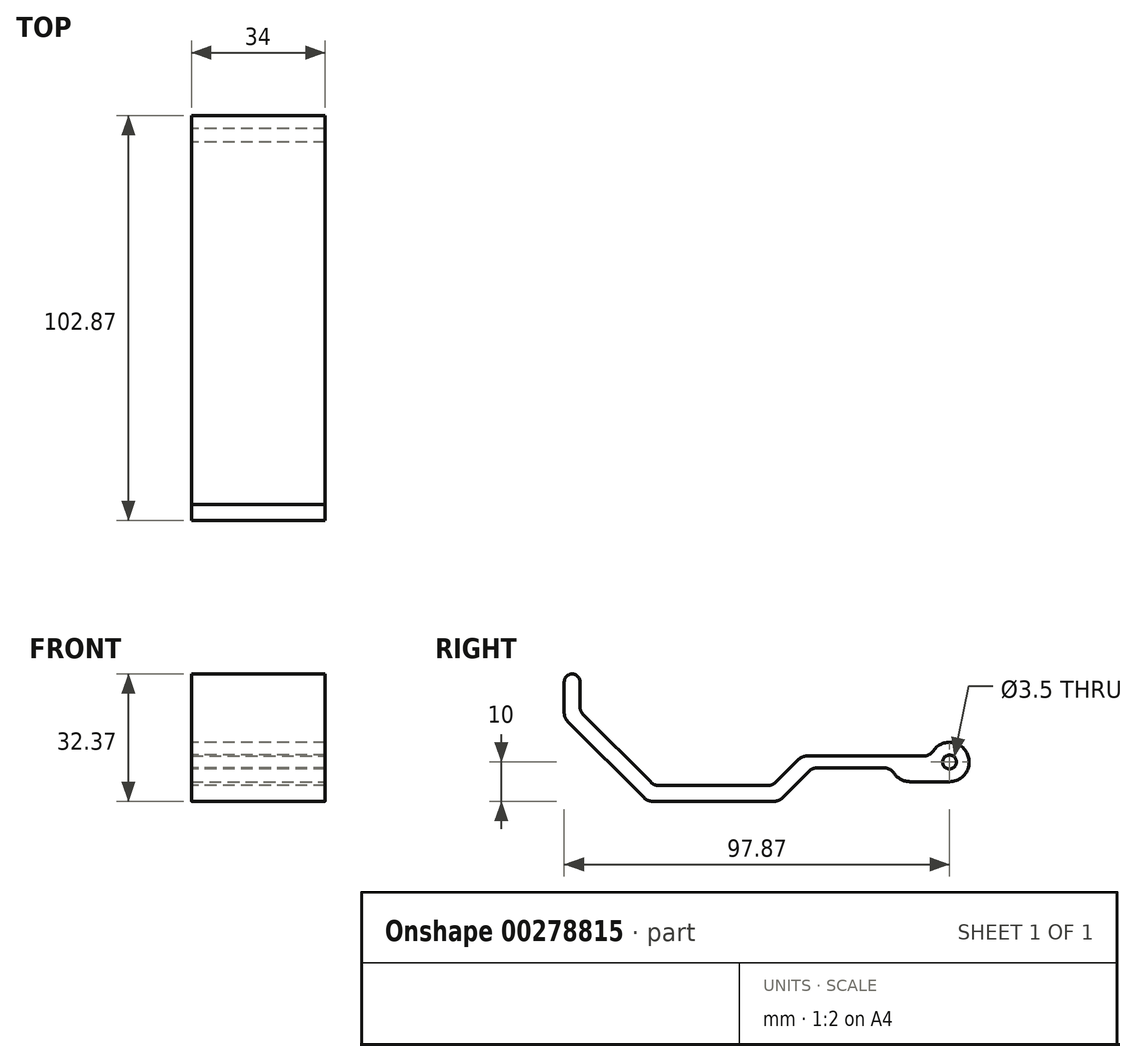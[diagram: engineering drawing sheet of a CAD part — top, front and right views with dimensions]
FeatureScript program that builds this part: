
annotation { "Feature Type Name" : "Feature", "Feature Type Description" : "" }
export const myFeature = defineFeature(function(context is Context, id is Id, definition is map)
    precondition{}
    {
        {
            var Q0;
            Q0=qCreatedBy(makeId("Right.planeOp"),FACE);
            var sketch = newSketch(context, id + "F0", { "sketchPlane" : qUnion([Q0])});
            skCircle(sketch, "E0", {"center": v(0, 0) * mm, "radius": 1.75 * mm});
            skLineSegment(sketch, "E1", {"start": v(0, 0) * mm, "end": v(-10, 0) * mm, "construction": true});
            skLineSegment(sketch, "E2", {"start": v(-10, 0) * mm, "end": v(-60, 0) * mm, "construction": true});
            skPoint(sketch, "E3", {"position": v(-42.5, 0) * mm});
            skLineSegment(sketch, "E4", {"start": v(-60, 0) * mm, "end": v(-60, 34.1) * mm, "construction": true});
            skCircle(sketch, "E5", {"center": v(-10, 0) * mm, "radius": 5 * mm, "construction": true});
            skArc(sketch, "E6", {"start": v(-4.77, -1.5) * mm, "mid": v(5, 0) * mm, "end": v(-4.77, 1.5) * mm});
            skLineSegment(sketch, "E7", {"start": v(-4.77, 1.5) * mm, "end": v(-37.5, 1.5) * mm});
            skLineSegment(sketch, "E8", {"start": v(-4.77, -1.5) * mm, "end": v(-5.23, -1.5) * mm});
            skArc(sketch, "E9", {"start": v(-5.23, -1.5) * mm, "mid": v(-10, -5) * mm, "end": v(-14.77, -1.5) * mm});
            skLineSegment(sketch, "E10", {"start": v(-75, -6) * mm, "end": v(-45, -6) * mm});
            skPoint(sketch, "E11", {"position": v(-60, -6) * mm});
            skLineSegment(sketch, "E12", {"start": v(-37.5, 1.5) * mm, "end": v(-45, -6) * mm});
            skLineSegment(sketch, "E13", {"start": v(-14.77, -1.5) * mm, "end": v(-34.84, -1.5) * mm});
            skLineSegment(sketch, "E14", {"start": v(-34.84, -1.5) * mm, "end": v(-43.34, -10) * mm});
            skLineSegment(sketch, "E15", {"start": v(-43.34, -10) * mm, "end": v(-76.66, -10) * mm});
            skLineSegment(sketch, "E16", {"start": v(-75, -6) * mm, "end": v(-93.87, 12.87) * mm});
            skLineSegment(sketch, "E17", {"start": v(-76.66, -10) * mm, "end": v(-97.87, 11.21) * mm});
            skLineSegment(sketch, "E18", {"start": v(-97.87, 11.21) * mm, "end": v(-97.87, 20.37) * mm});
            skLineSegment(sketch, "E19", {"start": v(-93.87, 12.87) * mm, "end": v(-93.87, 20.37) * mm});
            skArc(sketch, "E20", {"start": v(-93.87, 20.37) * mm, "mid": v(-95.87, 22.37) * mm, "end": v(-97.87, 20.37) * mm});
            skSolve(sketch);
        }
        {
            var Q0;
            Q0=qSketchRegion(id+"F0",true);
            extrude(context, id + "F1", {"entities" : qUnion([Q0]), "endBound" : BoundingType.SYMMETRIC, "depth" : 35 * mm});
        }
        {
            var Q0;
            Q0=makeQuery(id+"F1.opExtrude","CAP_FACE",FACE,{"disambiguationData":[OSD([sQuery(id+"F0.wireOp",EDGE,"E0"),sQuery(id+"F0.wireOp",EDGE,"E6"),sQuery(id+"F0.wireOp",EDGE,"E7"),sQuery(id+"F0.wireOp",EDGE,"E8"),sQuery(id+"F0.wireOp",EDGE,"E9"),sQuery(id+"F0.wireOp",EDGE,"E10"),sQuery(id+"F0.wireOp",EDGE,"E12"),sQuery(id+"F0.wireOp",EDGE,"E13"),sQuery(id+"F0.wireOp",EDGE,"E14"),sQuery(id+"F0.wireOp",EDGE,"E15"),sQuery(id+"F0.wireOp",EDGE,"E16"),sQuery(id+"F0.wireOp",EDGE,"E17"),sQuery(id+"F0.wireOp",EDGE,"00bbb578-9d78-4f2f-b791-4816d6ae5a66")])],"isStart":false});
            var sketch = newSketch(context, id + "F2", { "sketchPlane" : qUnion([Q0])});
            skLineSegment(sketch, "E21", {"start": v(-10, -5) * mm, "end": v(0, -5) * mm});
            skArc(sketch, "E22.0", {"start": v(-5.23, -1.5) * mm, "mid": v(-7.04, -4.03) * mm, "end": v(-10, -5) * mm});
            skArc(sketch, "E22.1", {"start": v(-4.77, -1.5) * mm, "mid": v(-2.96, -4.03) * mm, "end": v(0, -5) * mm});
            skLineSegment(sketch, "E22.2", {"start": v(-4.77, -1.5) * mm, "end": v(-5.23, -1.5) * mm});
            skPoint(sketch, "E23.orphan", {"position": v(-14.77, -1.5) * mm});
            skPoint(sketch, "E24.orphan", {"position": v(-4.77, 1.5) * mm});
            skSolve(sketch);
        }
        {
            var Q0;
            Q0=qSketchRegion(id+"F2",true);
            var Q1;
            Q1=makeQuery(id+"F1.opExtrude","CAP_FACE",FACE,{"disambiguationData":[OSD([sQuery(id+"F0.wireOp",EDGE,"E0"),sQuery(id+"F0.wireOp",EDGE,"E6"),sQuery(id+"F0.wireOp",EDGE,"E7"),sQuery(id+"F0.wireOp",EDGE,"E8"),sQuery(id+"F0.wireOp",EDGE,"E9"),sQuery(id+"F0.wireOp",EDGE,"E10"),sQuery(id+"F0.wireOp",EDGE,"E12"),sQuery(id+"F0.wireOp",EDGE,"E13"),sQuery(id+"F0.wireOp",EDGE,"E14"),sQuery(id+"F0.wireOp",EDGE,"E15"),sQuery(id+"F0.wireOp",EDGE,"E16"),sQuery(id+"F0.wireOp",EDGE,"E17"),sQuery(id+"F0.wireOp",EDGE,"00bbb578-9d78-4f2f-b791-4816d6ae5a66")])],"isStart":true});
            extrude(context, id + "F3", {"entities" : qUnion([Q0]), "operationType" : NewBodyOperationType.ADD, "endBound" : BoundingType.UP_TO_SURFACE, "oppositeDirection" : true, "endBoundEntityFace" : qUnion([Q1]), "depth" : 25 * mm});
        }
        {
            var Q0;
            Q0=makeQuery(id+"F1.opExtrude","SWEPT_EDGE",EDGE,{"disambiguationData":[OSD([sQuery(id+"F0.wireOp",EDGE,"E6"),sQuery(id+"F0.wireOp",EDGE,"E7")])]});
            var Q1;
            Q1=makeQuery(id+"F1.opExtrude","SWEPT_EDGE",EDGE,{"disambiguationData":[OSD([sQuery(id+"F0.wireOp",EDGE,"E9"),sQuery(id+"F0.wireOp",EDGE,"E13")])]});
            var Q2;
            Q2=makeQuery(id+"F1.opExtrude","SWEPT_EDGE",EDGE,{"disambiguationData":[OSD([sQuery(id+"F0.wireOp",EDGE,"E10"),sQuery(id+"F0.wireOp",EDGE,"E16")])]});
            var Q3;
            Q3=makeQuery(id+"F1.opExtrude","SWEPT_EDGE",EDGE,{"disambiguationData":[OSD([sQuery(id+"F0.wireOp",EDGE,"E15"),sQuery(id+"F0.wireOp",EDGE,"E17")])]});
            var Q4;
            Q4=makeQuery(id+"F1.opExtrude","SWEPT_EDGE",EDGE,{"disambiguationData":[OSD([sQuery(id+"F0.wireOp",EDGE,"E14"),sQuery(id+"F0.wireOp",EDGE,"E15")])]});
            var Q5;
            Q5=makeQuery(id+"F1.opExtrude","SWEPT_EDGE",EDGE,{"disambiguationData":[OSD([sQuery(id+"F0.wireOp",EDGE,"E13"),sQuery(id+"F0.wireOp",EDGE,"E14")])]});
            var Q6;
            Q6=makeQuery(id+"F1.opExtrude","SWEPT_EDGE",EDGE,{"disambiguationData":[OSD([sQuery(id+"F0.wireOp",EDGE,"E10"),sQuery(id+"F0.wireOp",EDGE,"E12")])]});
            var Q7;
            Q7=makeQuery(id+"F1.opExtrude","SWEPT_EDGE",EDGE,{"disambiguationData":[OSD([sQuery(id+"F0.wireOp",EDGE,"E7"),sQuery(id+"F0.wireOp",EDGE,"E12")])]});
            var Q8;
            Q8=makeQuery(id+"F1.opExtrude","SWEPT_EDGE",EDGE,{"disambiguationData":[OSD([sQuery(id+"F0.wireOp",EDGE,"E17"),sQuery(id+"F0.wireOp",EDGE,"E18")])]});
            var Q9;
            Q9=makeQuery(id+"F1.opExtrude","SWEPT_EDGE",EDGE,{"disambiguationData":[OSD([sQuery(id+"F0.wireOp",EDGE,"E16"),sQuery(id+"F0.wireOp",EDGE,"E19")])]});
            fillet(context, id + "F4", {"entities" : qUnion([Q0, Q1, Q2, Q3, Q4, Q5, Q6, Q7, Q8, Q9]), "radius" : 3 * mm, "tangentPropagation" : true, "allowEdgeOverflow" : false});
        }
        {
            var Q0;
            Q0=makeQuery(id+"F3.boolean.opBoolean","MERGE",FACE,{"derivedFrom":[makeQuery(id+"F1.opExtrude","CAP_FACE",FACE,{"disambiguationData":[OSD([sQuery(id+"F0.wireOp",EDGE,"E0"),sQuery(id+"F0.wireOp",EDGE,"E6"),sQuery(id+"F0.wireOp",EDGE,"E7"),sQuery(id+"F0.wireOp",EDGE,"E8"),sQuery(id+"F0.wireOp",EDGE,"E9"),sQuery(id+"F0.wireOp",EDGE,"E10"),sQuery(id+"F0.wireOp",EDGE,"E12"),sQuery(id+"F0.wireOp",EDGE,"E13"),sQuery(id+"F0.wireOp",EDGE,"E14"),sQuery(id+"F0.wireOp",EDGE,"E15"),sQuery(id+"F0.wireOp",EDGE,"E16"),sQuery(id+"F0.wireOp",EDGE,"E17"),sQuery(id+"F0.wireOp",EDGE,"00bbb578-9d78-4f2f-b791-4816d6ae5a66")])],"isStart":false}),makeQuery(id+"F3.opExtrude","CAP_FACE",FACE,{"disambiguationData":[OSD([sQuery(id+"F2.wireOp",EDGE,"E21"),sQuery(id+"F2.wireOp",EDGE,"E22.0"),sQuery(id+"F2.wireOp",EDGE,"E22.1"),sQuery(id+"F2.wireOp",EDGE,"E22.2")])],"isStart":true})]});
            extrude(context, id + "F5", {"entities" : qUnion([Q0]), "operationType" : NewBodyOperationType.REMOVE, "oppositeDirection" : true, "depth" : 0.5 * mm});
        }
        {
            var Q0;
            {var subQ0=sQuery(id+"F0.wireOp",EDGE,"00bbb578-9d78-4f2f-b791-4816d6ae5a66");var subQ1=sQuery(id+"F0.wireOp",EDGE,"E17");var subQ2=sQuery(id+"F0.wireOp",EDGE,"E16");var subQ3=sQuery(id+"F0.wireOp",EDGE,"E15");var subQ4=sQuery(id+"F0.wireOp",EDGE,"E14");var subQ5=sQuery(id+"F0.wireOp",EDGE,"E13");var subQ6=sQuery(id+"F0.wireOp",EDGE,"E12");var subQ7=sQuery(id+"F0.wireOp",EDGE,"E10");var subQ8=sQuery(id+"F0.wireOp",EDGE,"E9");var subQ9=sQuery(id+"F0.wireOp",EDGE,"E8");var subQ10=sQuery(id+"F0.wireOp",EDGE,"E7");var subQ11=sQuery(id+"F0.wireOp",EDGE,"E6");var subQ12=sQuery(id+"F0.wireOp",EDGE,"E0");Q0=makeQuery(id+"F3.boolean.opBoolean","MERGE",FACE,{"derivedFrom":[makeQuery(id+"F1.opExtrude","CAP_FACE",FACE,{"disambiguationData":[OSD([subQ12,subQ11,subQ10,subQ9,subQ8,subQ7,subQ6,subQ5,subQ4,subQ3,subQ2,subQ1,subQ0])],"isStart":true}),makeQuery(id+"F3.opExtrude","CAP_FACE",FACE,{"disambiguationData":[OSD([subQ12,subQ11,subQ10,subQ9,subQ8,subQ7,subQ6,subQ5,subQ4,subQ3,subQ2,subQ1,subQ0])],"isStart":false})]});}
            extrude(context, id + "F6", {"entities" : qUnion([Q0]), "operationType" : NewBodyOperationType.REMOVE, "oppositeDirection" : true, "depth" : 0.5 * mm});
        }
    });
